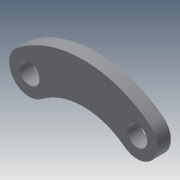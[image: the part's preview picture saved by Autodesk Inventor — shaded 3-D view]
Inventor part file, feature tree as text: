
AUTODESK INVENTOR PART (.ipt)
format: ipt  version: 2013 (Build 170138000, 138)  size: 90,112 bytes
history: native  units: mm
features: extrude x1, sketch x1
ambient origin geometry x8: Origin, YZ Plane, XZ Plane, XY Plane, X Axis, Y Axis, Z Axis, Center Point
bodies: Solid1 (feature_tree)
feature tree (2):
  extrude  "Extrusion1"  Depth=6.0mm
  sketch  "Sketch1"  dims[d13=16.0mm d14=6.0mm d16=6.0mm d17=3.0mm d18=3.0mm d19=2.0mm d20=0.0mm]
